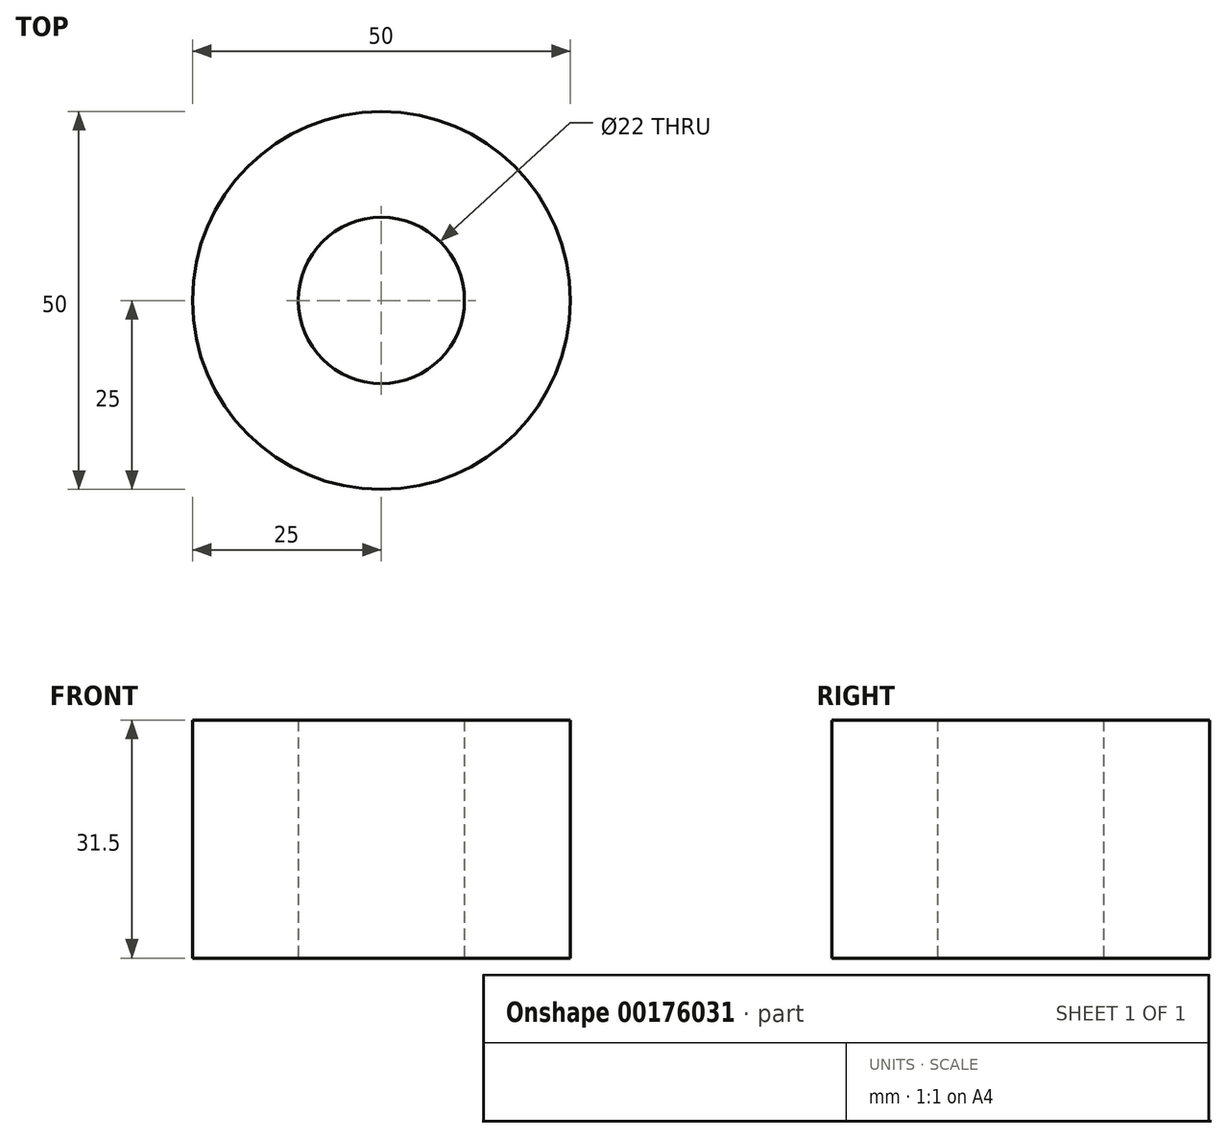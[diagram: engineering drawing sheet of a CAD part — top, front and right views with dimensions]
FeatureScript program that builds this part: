
annotation { "Feature Type Name" : "Feature", "Feature Type Description" : "" }
export const myFeature = defineFeature(function(context is Context, id is Id, definition is map)
    precondition{}
    {
        {
            var Q0;
            Q0=qCreatedBy(makeId("Top.planeOp"),FACE);
            var sketch = newSketch(context, id + "F0", { "sketchPlane" : qUnion([Q0])});
            skCircle(sketch, "E0", {"center": v(0, 0) * mm, "radius": 25 * mm});
            skCircle(sketch, "E1", {"center": v(0, 0) * mm, "radius": 11 * mm});
            skSolve(sketch);
        }
        {
            var Q0;
            Q0 = qSketchRegion(id + "F0", true);
            extrude(context, id + "F1", {"entities" : qUnion([Q0]), "depth" : 31.5 * mm});
        }
    });
